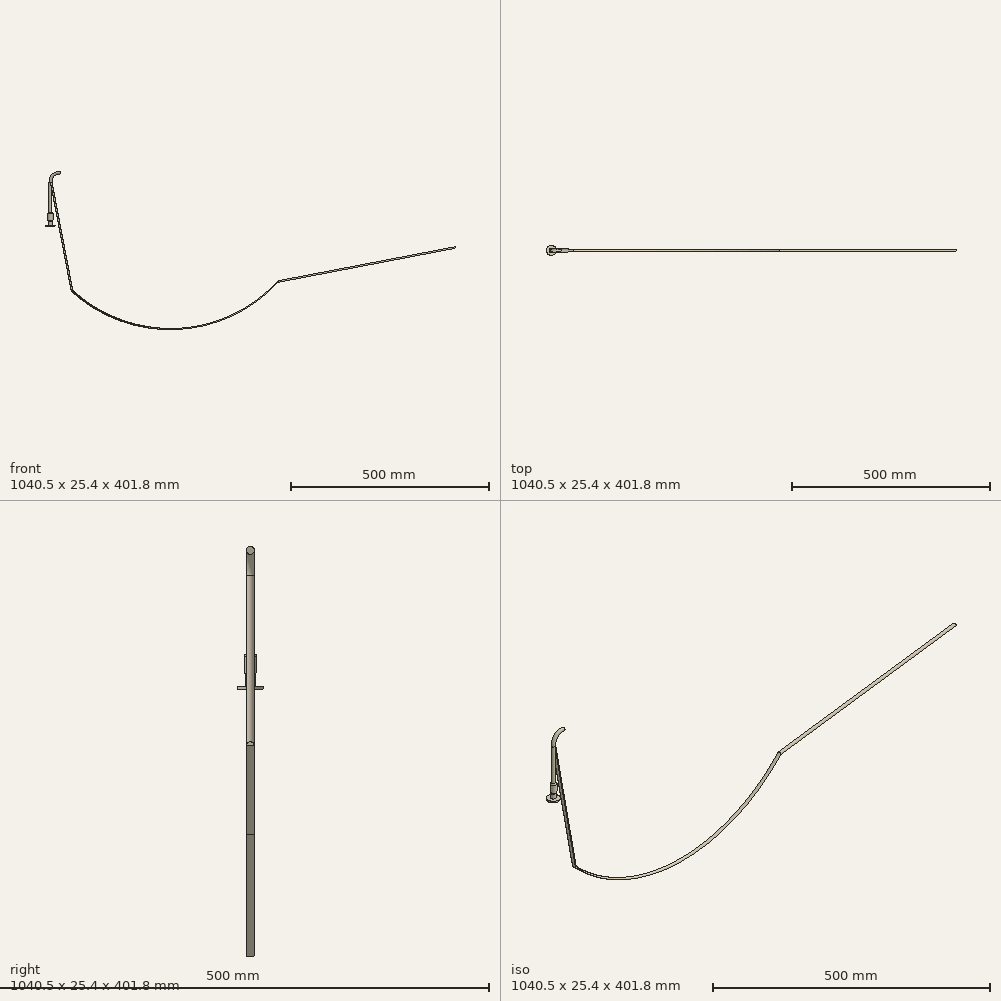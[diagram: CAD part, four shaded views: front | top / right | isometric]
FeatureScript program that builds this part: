
annotation { "Feature Type Name" : "Feature", "Feature Type Description" : "" }
export const myFeature = defineFeature(function(context is Context, id is Id, definition is map)
    precondition{}
    {
        {
            var Q0;
            Q0=qCreatedBy(makeId("Top.planeOp"),FACE);
            var sketch = newSketch(context, id + "F0", { "sketchPlane" : qUnion([Q0])});
            skCircle(sketch, "E0", {"center": v(0, 0) * mm, "radius": 12.7 * mm});
            skSolve(sketch);
        }
        {
            var Q0;
            Q0 = qSketchRegion(id + "F0", true);
            extrude(context, id + "F1", {"entities" : qUnion([Q0]), "depth" : 3.17 * mm});
        }
        {
            var Q0;
            Q0=makeQuery(id+"F1.opExtrude","CAP_FACE",FACE,{"disambiguationData":[OSD([sQuery(id+"F0.wireOp",EDGE,"E0")])],"isStart":false});
            var sketch = newSketch(context, id + "F2", { "sketchPlane" : qUnion([Q0])});
            skCircle(sketch, "E1", {"center": v(0, 0) * mm, "radius": 4.76 * mm});
            skSolve(sketch);
        }
        {
            var Q0;
            Q0 = qSketchRegion(id + "F2", true);
            extrude(context, id + "F3", {"entities" : qUnion([Q0]), "operationType" : NewBodyOperationType.ADD, "depth" : 12.7 * mm});
        }
        {
            var Q0;
            Q0=makeQuery(id+"F3.opExtrude","CAP_EDGE",EDGE,{"disambiguationData":[OSD([sQuery(id+"F2.wireOp",EDGE,"E1")])],"isStart":false});
            fillet(context, id + "F4", {"entities" : qUnion([Q0]), "radius" : 2.54 * mm, "allowEdgeOverflow" : false});
        }
        {
            var Q0;
            Q0=makeQuery(id+"F3.opExtrude","CAP_FACE",FACE,{"disambiguationData":[OSD([sQuery(id+"F2.wireOp",EDGE,"E1")])],"isStart":false});
            var sketch = newSketch(context, id + "F5", { "sketchPlane" : qUnion([Q0])});
            skCircle(sketch, "E2", {"center": v(0, 0) * mm, "radius": 6.35 * mm});
            skSolve(sketch);
        }
        {
            var Q0;
            Q0=makeQuery(id+"F5.imprint","IMPRINT",FACE,{"disambiguationData":[TD([[makeQuery(id+"F5.imprint","IMPRINT",EDGE,{"derivedFrom":sQuery(id+"F5.wireOp",EDGE,"E2")}),1.0]])]});
            extrude(context, id + "F6", {"entities" : qUnion([Q0]), "depth" : 19.05 * mm});
        }
        {
            var Q0;
            Q0=makeQuery(id+"F6.opExtrude","CAP_EDGE",EDGE,{"disambiguationData":[OSD([sQuery(id+"F5.wireOp",EDGE,"E2")])],"isStart":false});
            fillet(context, id + "F7", {"entities" : qUnion([Q0]), "radius" : 2.54 * mm, "tangentPropagation" : true, "allowEdgeOverflow" : false});
        }
        {
            var Q0;
            Q0=makeQuery(id+"F6.opExtrude","CAP_FACE",FACE,{"disambiguationData":[OSD([sQuery(id+"F2.wireOp",EDGE,"E1"),sQuery(id+"F5.wireOp",EDGE,"E2")])],"isStart":false});
            var sketch = newSketch(context, id + "F8", { "sketchPlane" : qUnion([Q0])});
            skCircle(sketch, "E3", {"center": v(0, 0) * mm, "radius": 3.81 * mm});
            skSolve(sketch);
        }
        {
            var Q0;
            Q0 = qSketchRegion(id + "F8", true);
            extrude(context, id + "F9", {"entities" : qUnion([Q0]), "operationType" : NewBodyOperationType.ADD, "depth" : 76.2 * mm});
        }
        {
            var Q0;
            Q0=qCreatedBy(makeId("Right.planeOp"),FACE);
            cPlane(context, id + "F10", {"entities" : qUnion([Q0]), "cplaneType" : CPlaneType.OFFSET, "offset" : 25.4 * mm, "width" : 152.4 * mm, "height" : 152.4 * mm});
        }
        {
            var Q0;
            Q0=qCreatedBy(id+"F10.planeOp",FACE);
            var sketch = newSketch(context, id + "F11", { "sketchPlane" : qUnion([Q0])});
            skLineSegment(sketch, "E4", {"start": v(0, 110.82) * mm, "end": v(0, 136.22) * mm, "construction": true});
            skCircle(sketch, "E5", {"center": v(0, 136.22) * mm, "radius": 3.81 * mm});
            skSolve(sketch);
        }
        {
            var Q0;
            Q0=qCreatedBy(makeId("Front.planeOp"),FACE);
            var sketch = newSketch(context, id + "F12", { "sketchPlane" : qUnion([Q0])});
            skArc(sketch, "E6", {"start": v(25.7, 136.33) * mm, "mid": v(6.86, 129.83) * mm, "end": v(0, 111.14) * mm});
            skSolve(sketch);
        }
        {
            var Q0;
            Q0=makeQuery(id+"F11.imprint","IMPRINT",FACE,{"disambiguationData":[TD([[makeQuery(id+"F11.imprint","IMPRINT",EDGE,{"derivedFrom":sQuery(id+"F11.wireOp",EDGE,"E5")}),1.0]])]});
            var Q1;
            Q1=sQuery(id+"F12.wireOp",EDGE,"E6");
            sweep(context, id + "F13", {"operationType" : NewBodyOperationType.ADD, "profiles" : qUnion([Q0]), "path" : qUnion([Q1])});
        }
        {
            var Q0;
            Q0=makeQuery(id+"F13.opSweep","CAP_FACE",FACE,{"disambiguationData":[OSD([sQuery(id+"F11.wireOp",EDGE,"E5"),sQuery(id+"F12.wireOp",VERTEX,"E6.start")])],"isStart":true});
            extrude(context, id + "F14", {"entities" : qUnion([Q0]), "operationType" : NewBodyOperationType.ADD, "depth" : 279.4 * mm});
        }
        {
            var Q0;
            Q0=qCreatedBy(makeId("Front.planeOp"),FACE);
            var sketch = newSketch(context, id + "F15", { "sketchPlane" : qUnion([Q0])});
            skArc(sketch, "E7", {"start": v(330.26, 110.73) * mm, "mid": v(322.82, 128.69) * mm, "end": v(304.86, 136.13) * mm});
            skLineSegment(sketch, "E8", {"start": v(304.86, 136.13) * mm, "end": v(330.26, 136.13) * mm, "construction": true});
            skLineSegment(sketch, "E9", {"start": v(330.26, 110.73) * mm, "end": v(330.26, 136.13) * mm, "construction": true});
            skSolve(sketch);
        }
        {
            var Q0;
            Q0=makeQuery(id+"F14.opExtrude","CAP_FACE",FACE,{"disambiguationData":[OSD([sQuery(id+"F11.wireOp",EDGE,"E5"),sQuery(id+"F12.wireOp",VERTEX,"E6.start")])],"isStart":false});
            var Q1;
            Q1=sQuery(id+"F15.wireOp",EDGE,"E7");
            sweep(context, id + "F16", {"operationType" : NewBodyOperationType.ADD, "profiles" : qUnion([Q0]), "path" : qUnion([Q1])});
        }
        {
            var Q0;
            Q0=makeQuery(id+"F16.opSweep","CAP_FACE",FACE,{"disambiguationData":[OSD([sQuery(id+"F11.wireOp",EDGE,"E5"),sQuery(id+"F12.wireOp",VERTEX,"E6.start"),sQuery(id+"F15.wireOp",VERTEX,"E7.start")])],"isStart":false});
            extrude(context, id + "F17", {"entities" : qUnion([Q0]), "depth" : 457.2 * mm});
        }
    });
